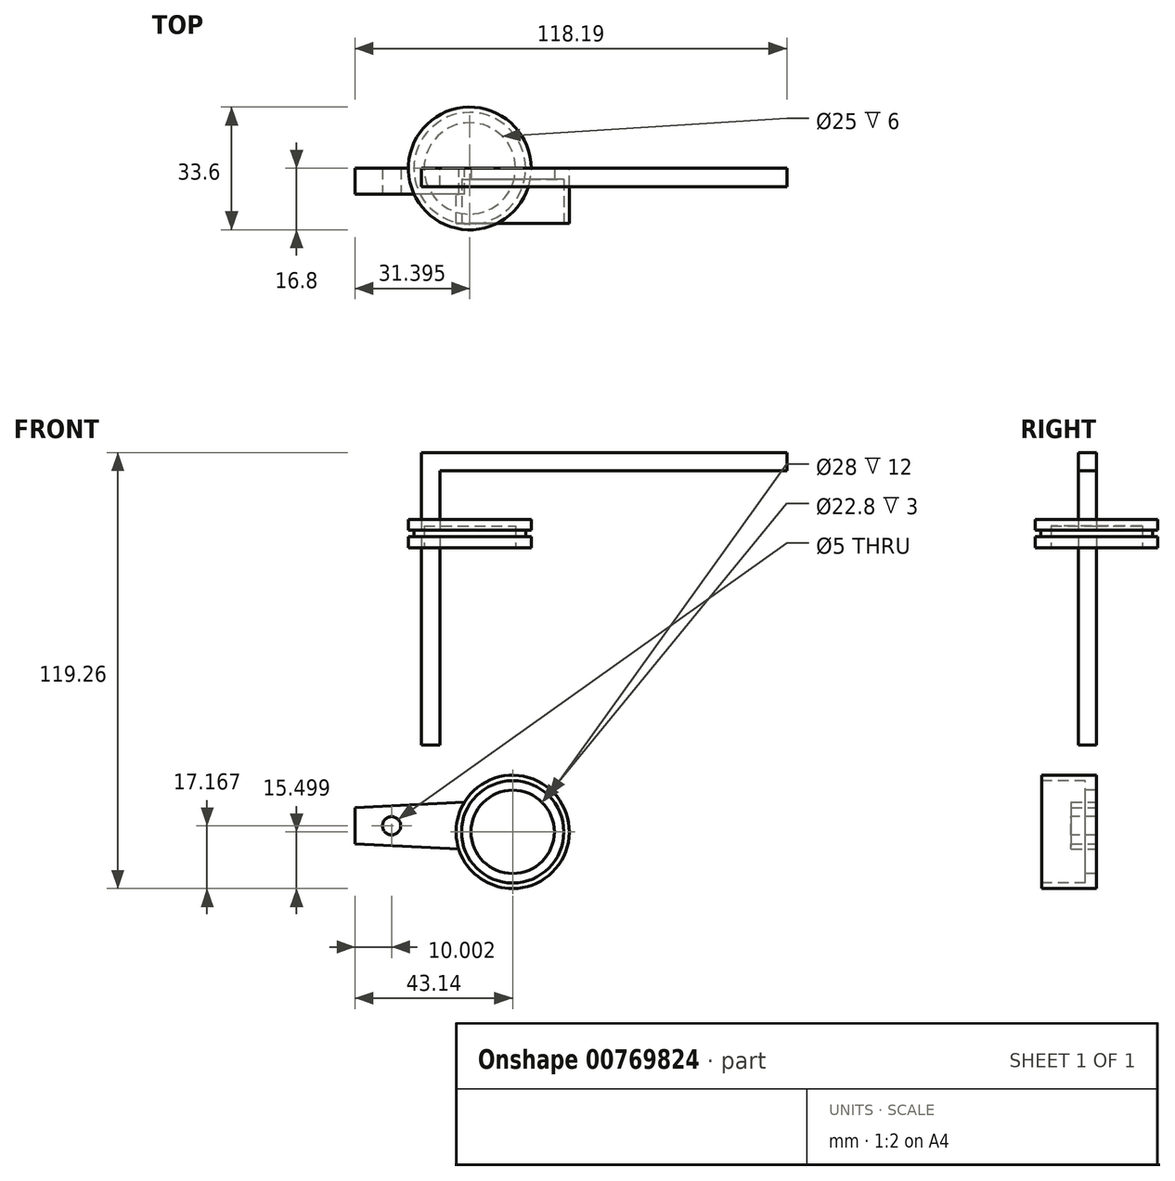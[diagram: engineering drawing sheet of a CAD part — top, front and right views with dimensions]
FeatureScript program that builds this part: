
annotation { "Feature Type Name" : "Feature", "Feature Type Description" : "" }
export const myFeature = defineFeature(function(context is Context, id is Id, definition is map)
    precondition{}
    {
        {
            var Q0;
            Q0=qCreatedBy(makeId("Front.planeOp"),FACE);
            var sketch = newSketch(context, id + "F0", { "sketchPlane" : qUnion([Q0])});
            skLineSegment(sketch, "E0", {"start": v(-28.55, 0) * mm, "end": v(-28.55, 3) * mm});
            skLineSegment(sketch, "E1", {"start": v(-28.55, 3) * mm, "end": v(-27.05, 3) * mm});
            skLineSegment(sketch, "E2", {"start": v(-27.05, 3) * mm, "end": v(-27.05, 4.8) * mm});
            skLineSegment(sketch, "E3", {"start": v(-27.05, 4.8) * mm, "end": v(-28.55, 4.8) * mm});
            skLineSegment(sketch, "E4", {"start": v(-28.55, 4.8) * mm, "end": v(-28.55, 7.8) * mm});
            skLineSegment(sketch, "E5", {"start": v(-11.75, 0) * mm, "end": v(-28.55, 0) * mm});
            skLineSegment(sketch, "E6", {"start": v(-28.55, 7.8) * mm, "end": v(-11.75, 7.8) * mm});
            skLineSegment(sketch, "E7", {"start": v(-11.75, 7.8) * mm, "end": v(-11.75, 0) * mm});
            skSolve(sketch);
        }
        {
            var Q0;
            Q0=makeQuery(id+"F0.imprint","IMPRINT",FACE,{"disambiguationData":[TD([[makeQuery(id+"F0.imprint","IMPRINT",EDGE,{"derivedFrom":sQuery(id+"F0.wireOp",EDGE,"E0")}),-1.0]])]});
            var Q1;
            Q1=sQuery(id+"F0.wireOp",EDGE,"E7");
            revolve(context, id + "F1", {"surfaceOperationType" : NewSurfaceOperationType.NEW, "entities" : qUnion([Q0]), "axis" : qUnion([Q1]), "revolveType" : RevolveType.FULL});
        }
        {
            var Q0;
            Q0=makeQuery(id+"F1.opRevolve","SWEPT_FACE",FACE,{"disambiguationData":[OSD([sQuery(id+"F0.wireOp",EDGE,"E5")])]});
            var sketch = newSketch(context, id + "F2", { "sketchPlane" : qUnion([Q0])});
            skCircle(sketch, "E8", {"center": v(-11.75, 0) * mm, "radius": 12.5 * mm});
            skSolve(sketch);
        }
        {
            var Q0;
            Q0=makeQuery(id+"F2.imprint","IMPRINT",FACE,{"disambiguationData":[TD([[makeQuery(id+"F2.imprint","IMPRINT",EDGE,{"derivedFrom":sQuery(id+"F2.wireOp",EDGE,"E8")}),1.0]])]});
            extrude(context, id + "F3", {"entities" : qUnion([Q0]), "operationType" : NewBodyOperationType.REMOVE, "oppositeDirection" : true, "depth" : 6 * mm, "offsetDistance" : 25 * mm});
        }
        {
            var Q0;
            Q0=qCreatedBy(makeId("Front.planeOp"),FACE);
            var sketch = newSketch(context, id + "F4", { "sketchPlane" : qUnion([Q0])});
            skCircle(sketch, "E9", {"center": v(0, -77.74) * mm, "radius": 15.5 * mm});
            skSolve(sketch);
        }
        {
            var Q0;
            Q0=makeQuery(id+"F4.imprint","IMPRINT",FACE,{"disambiguationData":[TD([[makeQuery(id+"F4.imprint","IMPRINT",EDGE,{"derivedFrom":sQuery(id+"F4.wireOp",EDGE,"E9")}),1.0]])]});
            extrude(context, id + "F5", {"entities" : qUnion([Q0]), "depth" : 15 * mm, "offsetDistance" : 25 * mm});
        }
        {
            var Q0;
            Q0=makeQuery(id+"F5.opExtrude","CAP_FACE",FACE,{"disambiguationData":[OSD([sQuery(id+"F4.wireOp",EDGE,"E9")])],"isStart":false});
            var sketch = newSketch(context, id + "F6", { "sketchPlane" : qUnion([Q0])});
            skCircle(sketch, "E10", {"center": v(0, -77.74) * mm, "radius": 14 * mm});
            skSolve(sketch);
        }
        {
            var Q0;
            Q0=makeQuery(id+"F6.imprint","IMPRINT",FACE,{"disambiguationData":[TD([[makeQuery(id+"F6.imprint","IMPRINT",EDGE,{"derivedFrom":sQuery(id+"F6.wireOp",EDGE,"E10")}),1.0]])]});
            extrude(context, id + "F7", {"entities" : qUnion([Q0]), "operationType" : NewBodyOperationType.REMOVE, "oppositeDirection" : true, "depth" : 12 * mm, "offsetDistance" : 25 * mm});
        }
        {
            var Q0;
            Q0=makeQuery(id+"F5.opExtrude","CAP_FACE",FACE,{"disambiguationData":[OSD([sQuery(id+"F4.wireOp",EDGE,"E9")])],"isStart":true});
            var sketch = newSketch(context, id + "F8", { "sketchPlane" : qUnion([Q0])});
            skLineSegment(sketch, "E11", {"start": v(13.18, -69.58) * mm, "end": v(43.14, -71.07) * mm});
            skLineSegment(sketch, "E12", {"start": v(43.14, -71.07) * mm, "end": v(43.14, -76.07) * mm});
            skLineSegment(sketch, "E13", {"start": v(43.14, -76.07) * mm, "end": v(15.4, -76.07) * mm});
            skLineSegment(sketch, "E14.MirrorCS", {"start": v(13.18, -82.57) * mm, "end": v(43.14, -81.07) * mm});
            skLineSegment(sketch, "E15.MirrorCS", {"start": v(43.14, -81.07) * mm, "end": v(43.14, -76.07) * mm});
            skSolve(sketch);
        }
        {
            var Q0;
            {var subQ0=sQuery(id+"F8.wireOp",EDGE,"E11");Q0=makeQuery(id+"F8.imprint","IMPRINT",FACE,{"disambiguationData":[TD([[makeQuery(id+"F8.imprint","IMPRINT",EDGE,{"derivedFrom":subQ0}),-1.0]])]});}
            var Q1;
            {var subQ0=sQuery(id+"F8.wireOp",EDGE,"E13");Q1=makeQuery(id+"F8.imprint","IMPRINT",FACE,{"disambiguationData":[TD([[makeQuery(id+"F8.imprint","IMPRINT",EDGE,{"derivedFrom":subQ0}),1.0]])]});}
            extrude(context, id + "F9", {"entities" : qUnion([Q0, Q1]), "operationType" : NewBodyOperationType.ADD, "oppositeDirection" : true, "depth" : 7 * mm, "offsetDistance" : 25 * mm});
        }
        {
            var Q0;
            Q0=makeQuery(id+"F7.boolean.opBoolean","COPY",FACE,{"derivedFrom":makeQuery(id+"F7.opExtrude","CAP_FACE",FACE,{"disambiguationData":[OSD([sQuery(id+"F6.wireOp",EDGE,"E10")])],"isStart":false})});
            var sketch = newSketch(context, id + "F10", { "sketchPlane" : qUnion([Q0])});
            skCircle(sketch, "E16", {"center": v(0, -77.74) * mm, "radius": 11.4 * mm});
            skSolve(sketch);
        }
        {
            var Q0;
            Q0=makeQuery(id+"F10.imprint","IMPRINT",FACE,{"disambiguationData":[TD([[makeQuery(id+"F10.imprint","IMPRINT",EDGE,{"derivedFrom":sQuery(id+"F10.wireOp",EDGE,"E16")}),1.0]])]});
            extrude(context, id + "F11", {"entities" : qUnion([Q0]), "operationType" : NewBodyOperationType.REMOVE, "oppositeDirection" : true, "depth" : 25 * mm, "offsetDistance" : 25 * mm});
        }
        {
            var Q0;
            Q0=makeQuery(id+"F9.opExtrude","CAP_FACE",FACE,{"disambiguationData":[OSD([sQuery(id+"F4.wireOp",EDGE,"E9"),sQuery(id+"F8.wireOp",EDGE,"E11"),sQuery(id+"F8.wireOp",EDGE,"E12"),sQuery(id+"F8.wireOp",EDGE,"E14.MirrorCS"),sQuery(id+"F8.wireOp",EDGE,"E15.MirrorCS")])],"isStart":false});
            var sketch = newSketch(context, id + "F12", { "sketchPlane" : qUnion([Q0])});
            skPoint(sketch, "E17", {"position": v(-33.14, -76.07) * mm});
            skPoint(sketch, "E17.positionSnap0", {"position": v(-43.14, -76.07) * mm});
            skSolve(sketch);
        }
        {
            var Q0;
            Q0=sQuery(id+"F12.wireOp",VERTEX,"E17");
            var Q1;
            Q1=makeQuery(id+"F5.opExtrude","SWEPT_BODY",BODY,{"disambiguationData":[OSD([sQuery(id+"F4.wireOp",EDGE,"E9")])]});
            hole(context, id + "F13", {"style" : HoleStyle.SIMPLE, "endStyle" : HoleEndStyle.THROUGH, "holeDiameter" : 5 * mm, "majorDiameter" : 5 * mm, "isTappedThrough" : true, "tappedDepth" : 12 * mm, "tapClearance" : 3, "startFromSketch" : true, "locations" : qUnion([Q0]), "scope" : qUnion([Q1])});
        }
        {
            var Q0;
            Q0=qCreatedBy(makeId("Front.planeOp"),FACE);
            var sketch = newSketch(context, id + "F14", { "sketchPlane" : qUnion([Q0])});
            skLineSegment(sketch, "E18.bottom", {"start": v(-24.95, 26.02) * mm, "end": v(75.05, 26.02) * mm});
            skLineSegment(sketch, "E18.top", {"start": v(-24.95, 21.02) * mm, "end": v(75.05, 21.02) * mm});
            skLineSegment(sketch, "E18.left", {"start": v(-24.95, 26.02) * mm, "end": v(-24.95, 21.02) * mm});
            skLineSegment(sketch, "E18.right", {"start": v(75.05, 26.02) * mm, "end": v(75.05, 21.02) * mm});
            skLineSegment(sketch, "E19.bottom", {"start": v(-24.95, 21.02) * mm, "end": v(-19.95, 21.02) * mm});
            skLineSegment(sketch, "E19.top", {"start": v(-24.95, -53.98) * mm, "end": v(-19.95, -53.98) * mm});
            skLineSegment(sketch, "E19.left", {"start": v(-24.95, 21.02) * mm, "end": v(-24.95, -53.98) * mm});
            skLineSegment(sketch, "E19.right", {"start": v(-19.95, 21.02) * mm, "end": v(-19.95, -53.98) * mm});
            skSolve(sketch);
        }
        {
            var Q0;
            Q0=makeQuery(id+"F14.imprint","IMPRINT",FACE,{"disambiguationData":[TD([[makeQuery(id+"F14.imprint","IMPRINT",EDGE,{"derivedFrom":sQuery(id+"F14.wireOp",EDGE,"E18.bottom")}),-1.0]])]});
            var Q1;
            Q1=makeQuery(id+"F14.imprint","IMPRINT",FACE,{"disambiguationData":[TD([[makeQuery(id+"F14.imprint","IMPRINT",EDGE,{"derivedFrom":sQuery(id+"F14.wireOp",EDGE,"E19.top")}),1.0]])]});
            extrude(context, id + "F15", {"entities" : qUnion([Q0, Q1]), "depth" : 5 * mm, "offsetDistance" : 25 * mm});
        }
    });
